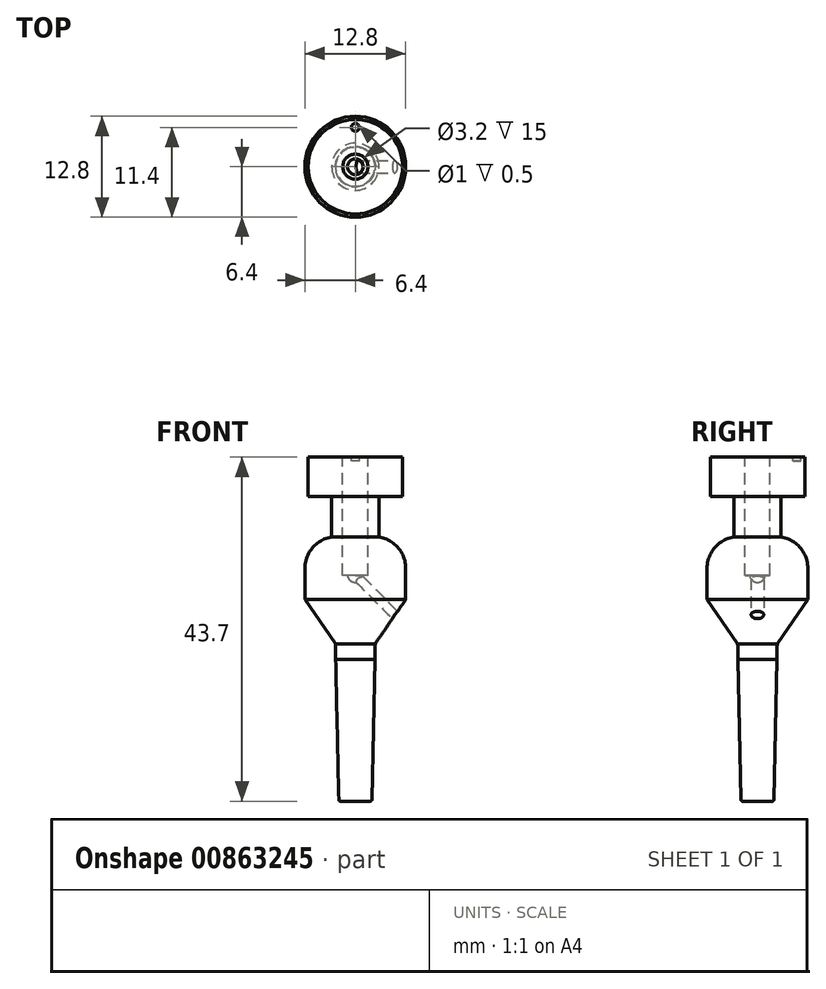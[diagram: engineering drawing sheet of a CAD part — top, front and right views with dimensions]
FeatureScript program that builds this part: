
annotation { "Feature Type Name" : "Feature", "Feature Type Description" : "" }
export const myFeature = defineFeature(function(context is Context, id is Id, definition is map)
    precondition{}
    {
        {
            var Q0;
            Q0=qCreatedBy(makeId("Front.planeOp"),FACE);
            var sketch = newSketch(context, id + "F0", { "sketchPlane" : qUnion([Q0])});
            skLineSegment(sketch, "E0", {"start": v(0, 0) * mm, "end": v(0, -20) * mm});
            skLineSegment(sketch, "E1", {"start": v(0, -20) * mm, "end": v(2.5, -20) * mm});
            skLineSegment(sketch, "E2", {"start": v(2.5, -20) * mm, "end": v(2.5, -0.32) * mm});
            skLineSegment(sketch, "E3", {"start": v(2.68, 0.26) * mm, "end": v(6.33, 5.48) * mm});
            skLineSegment(sketch, "E4", {"start": v(6.52, 6.05) * mm, "end": v(6.52, 9.73) * mm});
            skArc(sketch, "E5", {"start": v(6.52, 9.73) * mm, "mid": v(5.34, 12.57) * mm, "end": v(2.5, 13.73) * mm});
            skLineSegment(sketch, "E6", {"start": v(2.5, 13.73) * mm, "end": v(0, 13.72) * mm});
            skLineSegment(sketch, "E7", {"start": v(0, 0) * mm, "end": v(0, 13.72) * mm});
            skPoint(sketch, "E8.visualSharp", {"position": v(2.5, 0) * mm});
            skArc(sketch, "E8.filletArc", {"start": v(2.68, 0.26) * mm, "mid": v(2.55, -0.01) * mm, "end": v(2.5, -0.32) * mm});
            skPoint(sketch, "E9.visualSharp", {"position": v(6.52, 5.73) * mm});
            skArc(sketch, "E9.filletArc", {"start": v(6.33, 5.48) * mm, "mid": v(6.47, 5.75) * mm, "end": v(6.52, 6.05) * mm});
            skSolve(sketch);
        }
        {
            var Q0;
            Q0=makeQuery(id+"F0.imprint","IMPRINT",FACE,{"disambiguationData":[TD([[makeQuery(id+"F0.imprint","IMPRINT",EDGE,{"derivedFrom":sQuery(id+"F0.wireOp",EDGE,"E0")}),1.0]])]});
            var Q1;
            Q1=sQuery(id+"F0.wireOp",EDGE,"E7");
            revolve(context, id + "F1", {"surfaceOperationType" : NewSurfaceOperationType.NEW, "entities" : qUnion([Q0]), "axis" : qUnion([Q1]), "revolveType" : RevolveType.FULL});
        }
        {
            var Q0;
            Q0=qCreatedBy(makeId("Top.planeOp"),FACE);
            cPlane(context, id + "F2", {"entities" : qUnion([Q0]), "cplaneType" : CPlaneType.OFFSET, "offset" : 13.7 * mm, "width" : 150 * mm, "height" : 150 * mm});
        }
        {
            var Q0;
            Q0=qCreatedBy(makeId("Front.planeOp"),FACE);
            cPlane(context, id + "F3", {"entities" : qUnion([Q0]), "cplaneType" : CPlaneType.OFFSET, "offset" : 7 * mm, "width" : 150 * mm, "height" : 150 * mm});
        }
        {
            var Q0;
            Q0=qCreatedBy(id+"F3.planeOp",FACE);
            var sketch = newSketch(context, id + "F4", { "sketchPlane" : qUnion([Q0])});
            skLineSegment(sketch, "E10.bottom", {"start": v(-4.75, 11.8) * mm, "end": v(-5, 11.8) * mm});
            skLineSegment(sketch, "E10.top", {"start": v(-4.75, 5.8) * mm, "end": v(-5, 5.8) * mm});
            skLineSegment(sketch, "E10.left", {"start": v(-4.75, 11.8) * mm, "end": v(-4.75, 5.8) * mm});
            skLineSegment(sketch, "E10.right", {"start": v(-5, 11.8) * mm, "end": v(-5, 5.8) * mm});
            skLineSegment(sketch, "E11.1.0.0", {"start": v(-4, 11.8) * mm, "end": v(-4, 5.8) * mm});
            skLineSegment(sketch, "E11.1.0.1", {"start": v(-3.75, 11.8) * mm, "end": v(-3.75, 5.8) * mm});
            skLineSegment(sketch, "E11.1.0.2", {"start": v(-3.75, 5.8) * mm, "end": v(-4, 5.8) * mm});
            skLineSegment(sketch, "E11.1.0.3", {"start": v(-3.75, 11.8) * mm, "end": v(-4, 11.8) * mm});
            skLineSegment(sketch, "E11.2.0.0", {"start": v(-3, 11.8) * mm, "end": v(-3, 5.8) * mm});
            skLineSegment(sketch, "E11.2.0.1", {"start": v(-2.75, 11.8) * mm, "end": v(-2.75, 5.8) * mm});
            skLineSegment(sketch, "E11.2.0.2", {"start": v(-2.75, 5.8) * mm, "end": v(-3, 5.8) * mm});
            skLineSegment(sketch, "E11.2.0.3", {"start": v(-2.75, 11.8) * mm, "end": v(-3, 11.8) * mm});
            skLineSegment(sketch, "E11.3.0.0", {"start": v(-2, 11.8) * mm, "end": v(-2, 5.8) * mm});
            skLineSegment(sketch, "E11.3.0.1", {"start": v(-1.75, 11.8) * mm, "end": v(-1.75, 5.8) * mm});
            skLineSegment(sketch, "E11.3.0.2", {"start": v(-1.75, 5.8) * mm, "end": v(-2, 5.8) * mm});
            skLineSegment(sketch, "E11.3.0.3", {"start": v(-1.75, 11.8) * mm, "end": v(-2, 11.8) * mm});
            skLineSegment(sketch, "E11.4.0.0", {"start": v(-1, 11.8) * mm, "end": v(-1, 5.8) * mm});
            skLineSegment(sketch, "E11.4.0.1", {"start": v(-0.75, 11.8) * mm, "end": v(-0.75, 5.8) * mm});
            skLineSegment(sketch, "E11.4.0.2", {"start": v(-0.75, 5.8) * mm, "end": v(-1, 5.8) * mm});
            skLineSegment(sketch, "E11.4.0.3", {"start": v(-0.75, 11.8) * mm, "end": v(-1, 11.8) * mm});
            skLineSegment(sketch, "E11.5.0.0", {"start": v(0, 11.8) * mm, "end": v(0, 5.8) * mm});
            skLineSegment(sketch, "E11.5.0.1", {"start": v(0.25, 11.8) * mm, "end": v(0.25, 5.8) * mm});
            skLineSegment(sketch, "E11.5.0.2", {"start": v(0.25, 5.8) * mm, "end": v(0, 5.8) * mm});
            skLineSegment(sketch, "E11.5.0.3", {"start": v(0.25, 11.8) * mm, "end": v(0, 11.8) * mm});
            skLineSegment(sketch, "E11.6.0.0", {"start": v(1, 11.8) * mm, "end": v(1, 5.8) * mm});
            skLineSegment(sketch, "E11.6.0.1", {"start": v(1.25, 11.8) * mm, "end": v(1.25, 5.8) * mm});
            skLineSegment(sketch, "E11.6.0.2", {"start": v(1.25, 5.8) * mm, "end": v(1, 5.8) * mm});
            skLineSegment(sketch, "E11.6.0.3", {"start": v(1.25, 11.8) * mm, "end": v(1, 11.8) * mm});
            skLineSegment(sketch, "E11.7.0.0", {"start": v(2, 11.8) * mm, "end": v(2, 5.8) * mm});
            skLineSegment(sketch, "E11.7.0.1", {"start": v(2.25, 11.8) * mm, "end": v(2.25, 5.8) * mm});
            skLineSegment(sketch, "E11.7.0.2", {"start": v(2.25, 5.8) * mm, "end": v(2, 5.8) * mm});
            skLineSegment(sketch, "E11.7.0.3", {"start": v(2.25, 11.8) * mm, "end": v(2, 11.8) * mm});
            skLineSegment(sketch, "E11.8.0.0", {"start": v(3, 11.8) * mm, "end": v(3, 5.8) * mm});
            skLineSegment(sketch, "E11.8.0.1", {"start": v(3.25, 11.8) * mm, "end": v(3.25, 5.8) * mm});
            skLineSegment(sketch, "E11.8.0.2", {"start": v(3.25, 5.8) * mm, "end": v(3, 5.8) * mm});
            skLineSegment(sketch, "E11.8.0.3", {"start": v(3.25, 11.8) * mm, "end": v(3, 11.8) * mm});
            skLineSegment(sketch, "E11.9.0.0", {"start": v(4, 11.8) * mm, "end": v(4, 5.8) * mm});
            skLineSegment(sketch, "E11.9.0.1", {"start": v(4.25, 11.8) * mm, "end": v(4.25, 5.8) * mm});
            skLineSegment(sketch, "E11.9.0.2", {"start": v(4.25, 5.8) * mm, "end": v(4, 5.8) * mm});
            skLineSegment(sketch, "E11.9.0.3", {"start": v(4.25, 11.8) * mm, "end": v(4, 11.8) * mm});
            skLineSegment(sketch, "E11.10.0.0", {"start": v(5, 11.8) * mm, "end": v(5, 5.8) * mm});
            skLineSegment(sketch, "E11.10.0.1", {"start": v(5.25, 11.8) * mm, "end": v(5.25, 5.8) * mm});
            skLineSegment(sketch, "E11.10.0.2", {"start": v(5.25, 5.8) * mm, "end": v(5, 5.8) * mm});
            skLineSegment(sketch, "E11.10.0.3", {"start": v(5.25, 11.8) * mm, "end": v(5, 11.8) * mm});
            skLineSegment(sketch, "E11.direction1", {"start": v(-5, 5.8) * mm, "end": v(-4, 5.8) * mm, "construction": true});
            skLineSegment(sketch, "E11.direction2", {"start": v(-5, 5.8) * mm, "end": v(-5, 3.8) * mm, "construction": true});
            skSolve(sketch);
        }
        {
            var Q0;
            Q0=qSketchRegion(id+"F4",true);
            extrude(context, id + "F5", {"entities" : qUnion([Q0]), "operationType" : NewBodyOperationType.ADD, "oppositeDirection" : true, "depth" : 14.3 * mm, "offsetDistance" : 25 * mm});
        }
        {
            var Q0;
            Q0=qCreatedBy(makeId("Right.planeOp"),FACE);
            var sketch = newSketch(context, id + "F6", { "sketchPlane" : qUnion([Q0])});
            skLineSegment(sketch, "E12", {"start": v(-2.5, 0) * mm, "end": v(-6.4, 5.6) * mm});
            skLineSegment(sketch, "E13", {"start": v(-6.4, 5.6) * mm, "end": v(-6.4, 9.6) * mm});
            skArc(sketch, "E14", {"start": v(-2.4, 13.6) * mm, "mid": v(-5.23, 12.43) * mm, "end": v(-6.4, 9.6) * mm});
            skLineSegment(sketch, "E15", {"start": v(-2.4, 13.6) * mm, "end": v(-2.4, 16) * mm});
            skLineSegment(sketch, "E16", {"start": v(-2.4, 16) * mm, "end": v(-14.4, 16) * mm});
            skLineSegment(sketch, "E17", {"start": v(-14.4, 16) * mm, "end": v(-14.5, 0) * mm});
            skLineSegment(sketch, "E18", {"start": v(-14.5, 0) * mm, "end": v(-2.5, 0) * mm});
            skSolve(sketch);
        }
        {
            var Q0;
            Q0=qCreatedBy(makeId("Right.planeOp"),FACE);
            var sketch = newSketch(context, id + "F7", { "sketchPlane" : qUnion([Q0])});
            skLineSegment(sketch, "E19", {"start": v(0, -8.71) * mm, "end": v(0, 18.1) * mm, "construction": true});
            skSolve(sketch);
        }
        {
            var Q0;
            Q0=makeQuery(id+"F6.imprint","IMPRINT",FACE,{"disambiguationData":[TD([[makeQuery(id+"F6.imprint","IMPRINT",EDGE,{"derivedFrom":sQuery(id+"F6.wireOp",EDGE,"E12")}),1.0]])]});
            var Q1;
            Q1=sQuery(id+"F7.wireOp",EDGE,"E19");
            var Q2;
            Q2=sQuery(id+"F7.wireOp",EDGE,"E19");
            revolve(context, id + "F8", {"operationType" : NewBodyOperationType.REMOVE, "surfaceOperationType" : NewSurfaceOperationType.NEW, "entities" : qUnion([Q0]), "surfaceEntities" : qUnion([Q1]), "axis" : qUnion([Q2]), "revolveType" : RevolveType.FULL, "oppositeDirection" : true});
        }
        {
            var Q0;
            Q0=qCreatedBy(id+"F2.planeOp",FACE);
            var sketch = newSketch(context, id + "F9", { "sketchPlane" : qUnion([Q0])});
            skCircle(sketch, "E20", {"center": v(0, 0) * mm, "radius": 3 * mm});
            skSolve(sketch);
        }
        {
            var Q0;
            Q0=qSketchRegion(id+"F9",true);
            extrude(context, id + "F10", {"entities" : qUnion([Q0]), "operationType" : NewBodyOperationType.ADD, "depth" : 10 * mm, "offsetDistance" : 25 * mm, "hasSecondDirection" : true, "secondDirectionOppositeDirection" : true, "secondDirectionDepth" : 1 * mm});
        }
        {
            var Q0;
            Q0=makeQuery(id+"F10.opExtrude","CAP_FACE",FACE,{"disambiguationData":[OSD([sQuery(id+"F9.wireOp",EDGE,"E20")])],"isStart":false});
            var sketch = newSketch(context, id + "F11", { "sketchPlane" : qUnion([Q0])});
            skCircle(sketch, "E21", {"center": v(0, 0) * mm, "radius": 1.6 * mm});
            skSolve(sketch);
        }
        {
            var Q0;
            Q0=makeQuery(id+"F11.imprint","IMPRINT",FACE,{"disambiguationData":[TD([[makeQuery(id+"F11.imprint","IMPRINT",EDGE,{"derivedFrom":sQuery(id+"F11.wireOp",EDGE,"E21")}),1.0]])]});
            var Q1;
            Q1=sQuery(id+"F11.wireOp",EDGE,"E21");
            extrude(context, id + "F12", {"entities" : qUnion([Q0]), "operationType" : NewBodyOperationType.REMOVE, "surfaceEntities" : qUnion([Q1]), "oppositeDirection" : true, "depth" : 15 * mm, "offsetDistance" : 25 * mm});
        }
        {
            var Q0;
            Q0=qCreatedBy(makeId("Front.planeOp"),FACE);
            var sketch = newSketch(context, id + "F13", { "sketchPlane" : qUnion([Q0])});
            skLineSegment(sketch, "E22", {"start": v(0, 8.7) * mm, "end": v(5.5, 3.2) * mm});
            skSolve(sketch);
        }
        {
            var Q0;
            Q0=qCreatedBy(makeId("Right.planeOp"),FACE);
            cPlane(context, id + "F14", {"entities" : qUnion([Q0]), "cplaneType" : CPlaneType.OFFSET, "offset" : 5.5 * mm, "width" : 150 * mm, "height" : 150 * mm});
        }
        {
            var Q0;
            Q0=qCreatedBy(id+"F14.planeOp",FACE);
            var sketch = newSketch(context, id + "F15", { "sketchPlane" : qUnion([Q0])});
            skCircle(sketch, "E23", {"center": v(0, 3.2) * mm, "radius": 1 * mm});
            skSolve(sketch);
        }
        {
            var Q0;
            Q0=makeQuery(id+"F15.imprint","IMPRINT",FACE,{"disambiguationData":[TD([[makeQuery(id+"F15.imprint","IMPRINT",EDGE,{"derivedFrom":sQuery(id+"F15.wireOp",EDGE,"E23")}),1.0]])]});
            var Q1;
            Q1=sQuery(id+"F13.wireOp",EDGE,"E22");
            sweep(context, id + "F16", {"operationType" : NewBodyOperationType.REMOVE, "profiles" : qUnion([Q0]), "path" : qUnion([Q1])});
        }
        {
            var Q0;
            Q0=qCreatedBy(makeId("Front.planeOp"),FACE);
            var sketch = newSketch(context, id + "F17", { "sketchPlane" : qUnion([Q0])});
            skLineSegment(sketch, "E24", {"start": v(0, 8.7) * mm, "end": v(5.5, 3.2) * mm});
            skSolve(sketch);
        }
        {
            var Q0;
            Q0=qCreatedBy(id+"F14.planeOp",FACE);
            var sketch = newSketch(context, id + "F18", { "sketchPlane" : qUnion([Q0])});
            skCircle(sketch, "E25", {"center": v(0, 3.2) * mm, "radius": 1 * mm});
            skCircle(sketch, "E26", {"center": v(0, 3.2) * mm, "radius": 0.8 * mm});
            skSolve(sketch);
        }
        {
            var Q0;
            Q0=qSketchRegion(id+"F18",true);
            var Q1;
            Q1=sQuery(id+"F17.wireOp",EDGE,"E24");
            sweep(context, id + "F19", {"operationType" : NewBodyOperationType.ADD, "profiles" : qUnion([Q0]), "path" : qUnion([Q1])});
        }
        {
            var Q0;
            Q0=qCreatedBy(makeId("Front.planeOp"),FACE);
            var sketch = newSketch(context, id + "F20", { "sketchPlane" : qUnion([Q0])});
            skArc(sketch, "E27", {"start": v(0, 7.79) * mm, "mid": v(1, 8.79) * mm, "end": v(0, 9.79) * mm});
            skLineSegment(sketch, "E28", {"start": v(0, 9.79) * mm, "end": v(0, 7.79) * mm});
            skSolve(sketch);
        }
        {
            var Q0;
            Q0=qCreatedBy(makeId("Front.planeOp"),FACE);
            var sketch = newSketch(context, id + "F21", { "sketchPlane" : qUnion([Q0])});
            skLineSegment(sketch, "E29", {"start": v(0, 12.3) * mm, "end": v(0, 5.36) * mm, "construction": true});
            skSolve(sketch);
        }
        {
            var Q0;
            Q0=makeQuery(id+"F20.imprint","IMPRINT",FACE,{"disambiguationData":[TD([[makeQuery(id+"F20.imprint","IMPRINT",EDGE,{"derivedFrom":sQuery(id+"F20.wireOp",EDGE,"E27")}),1.0]])]});
            var Q1;
            Q1=sQuery(id+"F21.wireOp",EDGE,"E29");
            revolve(context, id + "F22", {"operationType" : NewBodyOperationType.REMOVE, "surfaceOperationType" : NewSurfaceOperationType.NEW, "entities" : qUnion([Q0]), "axis" : qUnion([Q1]), "revolveType" : RevolveType.FULL, "oppositeDirection" : true});
        }
        {
            var Q0;
            Q0=qCreatedBy(makeId("Front.planeOp"),FACE);
            var sketch = newSketch(context, id + "F23", { "sketchPlane" : qUnion([Q0])});
            skLineSegment(sketch, "E30", {"start": v(2.5, 0) * mm, "end": v(6.4, 5.6) * mm});
            skArc(sketch, "E31", {"start": v(2.5, 0) * mm, "mid": v(7.26, 0.84) * mm, "end": v(6.4, 5.6) * mm});
            skSolve(sketch);
        }
        {
            var Q0;
            Q0=makeQuery(id+"F23.imprint","IMPRINT",FACE,{"disambiguationData":[TD([[makeQuery(id+"F23.imprint","IMPRINT",EDGE,{"derivedFrom":sQuery(id+"F23.wireOp",EDGE,"E30")}),-1.0]])]});
            var Q1;
            Q1=sQuery(id+"F21.wireOp",EDGE,"E29");
            revolve(context, id + "F24", {"operationType" : NewBodyOperationType.REMOVE, "surfaceOperationType" : NewSurfaceOperationType.NEW, "entities" : qUnion([Q0]), "axis" : qUnion([Q1]), "revolveType" : RevolveType.FULL, "oppositeDirection" : true});
        }
        {
            var Q0;
            Q0=makeQuery(id+"F10.opExtrude","CAP_FACE",FACE,{"disambiguationData":[OSD([sQuery(id+"F9.wireOp",EDGE,"E20")])],"isStart":false});
            var sketch = newSketch(context, id + "F25", { "sketchPlane" : qUnion([Q0])});
            skCircle(sketch, "E32", {"center": v(0, 0) * mm, "radius": 6 * mm});
            skCircle(sketch, "E33", {"center": v(0, 0) * mm, "radius": 2.6 * mm});
            skSolve(sketch);
        }
        {
            var Q0;
            Q0=qSketchRegion(id+"F25",true);
            extrude(context, id + "F26", {"entities" : qUnion([Q0]), "operationType" : NewBodyOperationType.ADD, "oppositeDirection" : true, "depth" : 5 * mm, "offsetDistance" : 25 * mm});
        }
        {
            var Q0;
            Q0=makeQuery(id+"F1.opRevolve","SWEPT_EDGE",EDGE,{"disambiguationData":[OSD([sQuery(id+"F0.wireOp",EDGE,"E1"),sQuery(id+"F0.wireOp",EDGE,"E2")])]});
            chamfer(context, id + "F27", {"entities" : qUnion([Q0]), "chamferType" : ChamferType.TWO_OFFSETS, "width1" : 0.4 * mm, "oppositeDirection" : false, "width2" : 18 * mm, "tangentPropagation" : true});
        }
        {
            var Q0;
            {var subQ0=sQuery(id+"F0.wireOp",EDGE,"E1");Q0=makeQuery(id+"F27.opChamfer","BLEND_EDGE",EDGE,{"blendedFrom":[makeQuery(id+"F1.opRevolve","SWEPT_EDGE",EDGE,{"disambiguationData":[OSD([subQ0,sQuery(id+"F0.wireOp",EDGE,"E2")])]}),makeQuery(id+"F1.opRevolve","SWEPT_FACE",FACE,{"disambiguationData":[OSD([subQ0])]})],"blendedInto":[makeQuery(id+"F1.opRevolve","SWEPT_FACE",FACE,{"disambiguationData":[OSD([subQ0])]})]});}
            fillet(context, id + "F28", {"entities" : qUnion([Q0]), "radius" : 0.2 * mm, "tangentPropagation" : true, "allowEdgeOverflow" : false});
        }
        {
            var Q0;
            Q0=makeQuery(id+"F26.boolean.opBoolean","MERGE",FACE,{"derivedFrom":[makeQuery(id+"F10.opExtrude","CAP_FACE",FACE,{"disambiguationData":[OSD([sQuery(id+"F9.wireOp",EDGE,"E20")])],"isStart":false}),makeQuery(id+"F26.opExtrude","CAP_FACE",FACE,{"disambiguationData":[OSD([sQuery(id+"F25.wireOp",EDGE,"E32"),sQuery(id+"F25.wireOp",EDGE,"E33")])],"isStart":true})]});
            var sketch = newSketch(context, id + "F29", { "sketchPlane" : qUnion([Q0])});
            skCircle(sketch, "E34", {"center": v(0, 5) * mm, "radius": 0.5 * mm});
            skSolve(sketch);
        }
        {
            var Q0;
            Q0 = qSketchRegion(id + "F29", true);
            extrude(context, id + "F30", {"entities" : qUnion([Q0]), "operationType" : NewBodyOperationType.REMOVE, "oppositeDirection" : true, "depth" : 0.5 * mm, "offsetDistance" : 25 * mm});
        }
        {
            var Q0;
            {var subQ0=sQuery(id+"F23.wireOp",EDGE,"E31");var subQ1=sQuery(id+"F23.wireOp",EDGE,"E30");Q0=makeQuery(id+"F24.boolean.opBoolean","MERGE",EDGE,{"derivedFrom":[makeQuery(id+"F8.boolean.opBoolean","COPY",EDGE,{"derivedFrom":makeQuery(id+"F8.opRevolve","SWEPT_EDGE",EDGE,{"disambiguationData":[OSD([sQuery(id+"F6.wireOp",EDGE,"E12"),sQuery(id+"F6.wireOp",EDGE,"E18")])]})}),makeQuery(id+"F24.opRevolve","SWEPT_EDGE",EDGE,{"disambiguationData":[OSD([subQ1,subQ0]),TDD([makeQuery(id+"F23.imprint","INTERSECT",VERTEX,{"disambiguationData":[OD(0.0)],"derivedFrom":[subQ1,subQ0]})])]})]});}
            fillet(context, id + "F31", {"entities" : qUnion([Q0]), "radius" : 0.2 * mm, "tangentPropagation" : true, "allowEdgeOverflow" : false});
        }
    });
